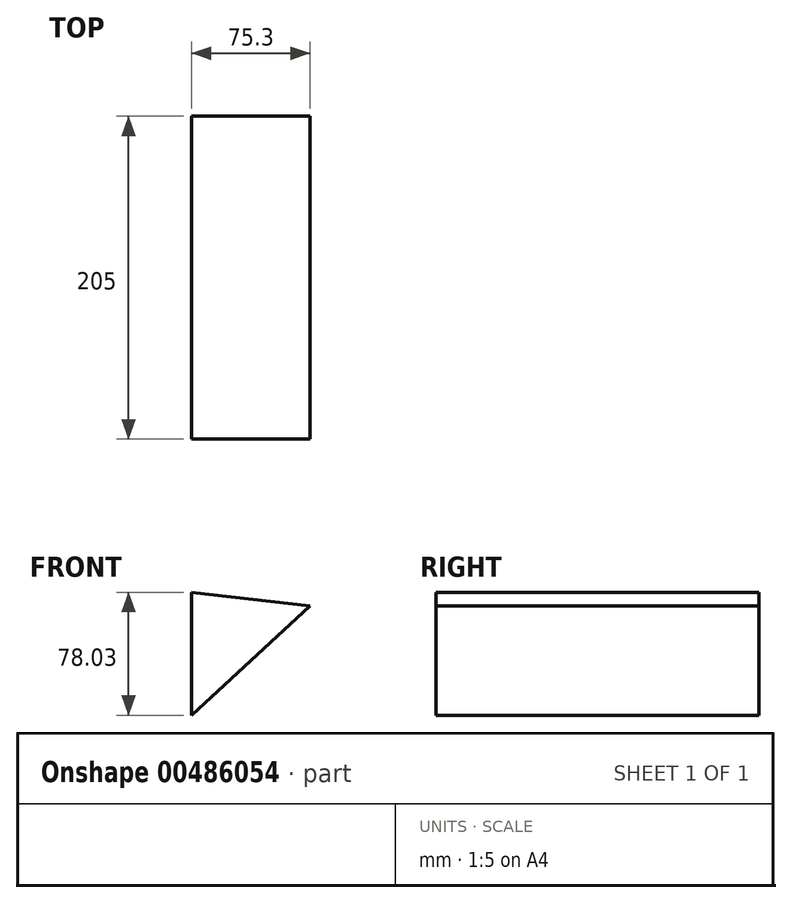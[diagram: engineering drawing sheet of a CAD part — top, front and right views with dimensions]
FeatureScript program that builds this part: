
annotation { "Feature Type Name" : "Feature", "Feature Type Description" : "" }
export const myFeature = defineFeature(function(context is Context, id is Id, definition is map)
    precondition{}
    {
        {
            var Q0;
            Q0=qCreatedBy(makeId("Front.planeOp"),FACE);
            var sketch = newSketch(context, id + "F0", { "sketchPlane" : qUnion([Q0])});
            skLineSegment(sketch, "E0", {"start": v(-59.5, 46.9) * mm, "end": v(-59.5, -31.14) * mm});
            skLineSegment(sketch, "E1", {"start": v(-59.5, -31.14) * mm, "end": v(15.8, 38.26) * mm});
            skLineSegment(sketch, "E2", {"start": v(-59.5, 46.9) * mm, "end": v(15.8, 38.26) * mm});
            skSolve(sketch);
        }
        {
            var Q0;
            Q0 = qSketchRegion(id + "F0", true);
            extrude(context, id + "F1", {"entities" : qUnion([Q0]), "depth" : 205 * mm});
        }
    });
